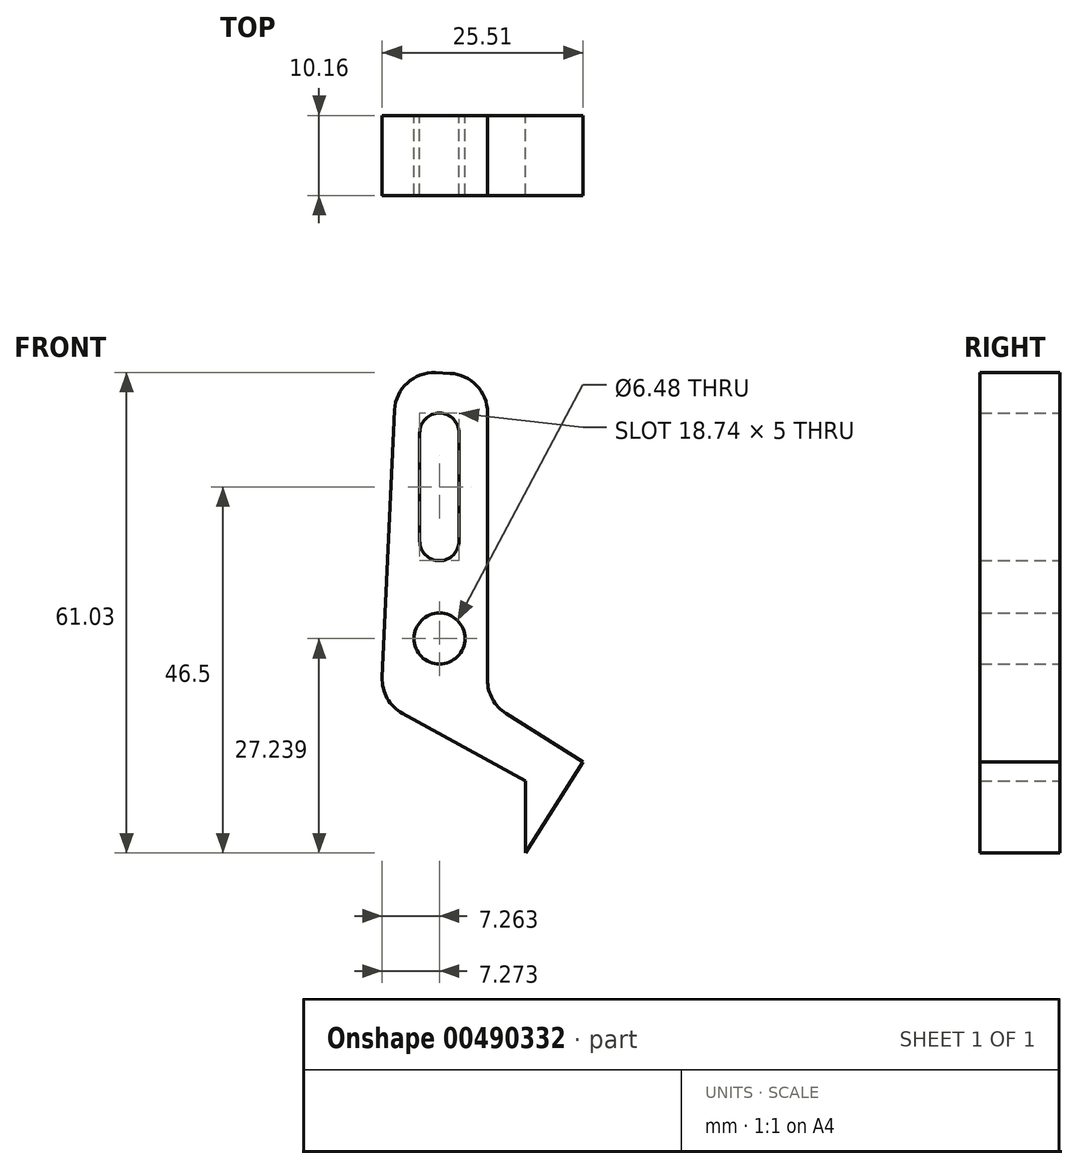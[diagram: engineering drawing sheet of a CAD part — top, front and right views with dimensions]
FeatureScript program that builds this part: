
annotation { "Feature Type Name" : "Feature", "Feature Type Description" : "" }
export const myFeature = defineFeature(function(context is Context, id is Id, definition is map)
    precondition{}
    {
        {
            var Q0;
            Q0=qCreatedBy(makeId("Front.planeOp"),FACE);
            var sketch = newSketch(context, id + "F0", { "sketchPlane" : qUnion([Q0])});
            skLineSegment(sketch, "E0", {"start": v(3.59, 36.06) * mm, "end": v(3.59, 18.53) * mm});
            skLineSegment(sketch, "E1", {"start": v(5.92, 14.3) * mm, "end": v(15.72, 8.12) * mm});
            skLineSegment(sketch, "E2", {"start": v(15.72, 8.12) * mm, "end": v(8.44, -3.44) * mm});
            skLineSegment(sketch, "E3", {"start": v(8.44, -3.44) * mm, "end": v(8.44, 5.7) * mm});
            skLineSegment(sketch, "E4", {"start": v(8.44, 5.7) * mm, "end": v(-7.2, 14.27) * mm});
            skLineSegment(sketch, "E5", {"start": v(-9.78, 18.88) * mm, "end": v(-8.23, 52.81) * mm});
            skLineSegment(sketch, "E6", {"start": v(-3, 57.58) * mm, "end": v(-1.19, 57.5) * mm});
            skLineSegment(sketch, "E7", {"start": v(3.59, 52.5) * mm, "end": v(3.59, 36.06) * mm});
            skPoint(sketch, "E8.visualSharp", {"position": v(-8, 57.8) * mm});
            skArc(sketch, "E8.filletArc", {"start": v(-3, 57.58) * mm, "mid": v(-6.6, 56.28) * mm, "end": v(-8.23, 52.81) * mm});
            skPoint(sketch, "E9.visualSharp", {"position": v(3.59, 57.28) * mm});
            skArc(sketch, "E9.filletArc", {"start": v(3.59, 52.5) * mm, "mid": v(2.2, 55.96) * mm, "end": v(-1.19, 57.5) * mm});
            skPoint(sketch, "E10.visualSharp", {"position": v(-9.93, 15.77) * mm});
            skArc(sketch, "E10.filletArc", {"start": v(-9.78, 18.88) * mm, "mid": v(-9.15, 16.2) * mm, "end": v(-7.2, 14.27) * mm});
            skPoint(sketch, "E11.visualSharp", {"position": v(3.59, 15.77) * mm});
            skArc(sketch, "E11.filletArc", {"start": v(3.59, 18.53) * mm, "mid": v(4.2, 16.11) * mm, "end": v(5.92, 14.3) * mm});
            skLineSegment(sketch, "E12", {"start": v(-2.53, 49.93) * mm, "end": v(-2.53, 36.19) * mm});
            skArc(sketch, "E13.0.startCap", {"start": v(-5.03, 49.93) * mm, "mid": v(-2.53, 52.43) * mm, "end": v(-0.03, 49.93) * mm});
            skArc(sketch, "E13.0.endCap", {"start": v(-0.03, 36.19) * mm, "mid": v(-2.53, 33.69) * mm, "end": v(-5.03, 36.19) * mm});
            skLineSegment(sketch, "E13.0.left", {"start": v(-0.03, 49.93) * mm, "end": v(-0.03, 36.19) * mm});
            skLineSegment(sketch, "E13.0.right", {"start": v(-5.03, 49.93) * mm, "end": v(-5.03, 36.19) * mm});
            skCircle(sketch, "E14", {"center": v(-2.52, 23.8) * mm, "radius": 3.24 * mm});
            skSolve(sketch);
        }
        {
            var Q0;
            Q0=makeQuery(id+"F0.imprint","IMPRINT",FACE,{"disambiguationData":[TD([[makeQuery(id+"F0.imprint","IMPRINT",EDGE,{"derivedFrom":sQuery(id+"F0.wireOp",EDGE,"E0")}),-1.0]])]});
            extrude(context, id + "F1", {"entities" : qUnion([Q0]), "depth" : 10.16 * mm});
        }
    });
